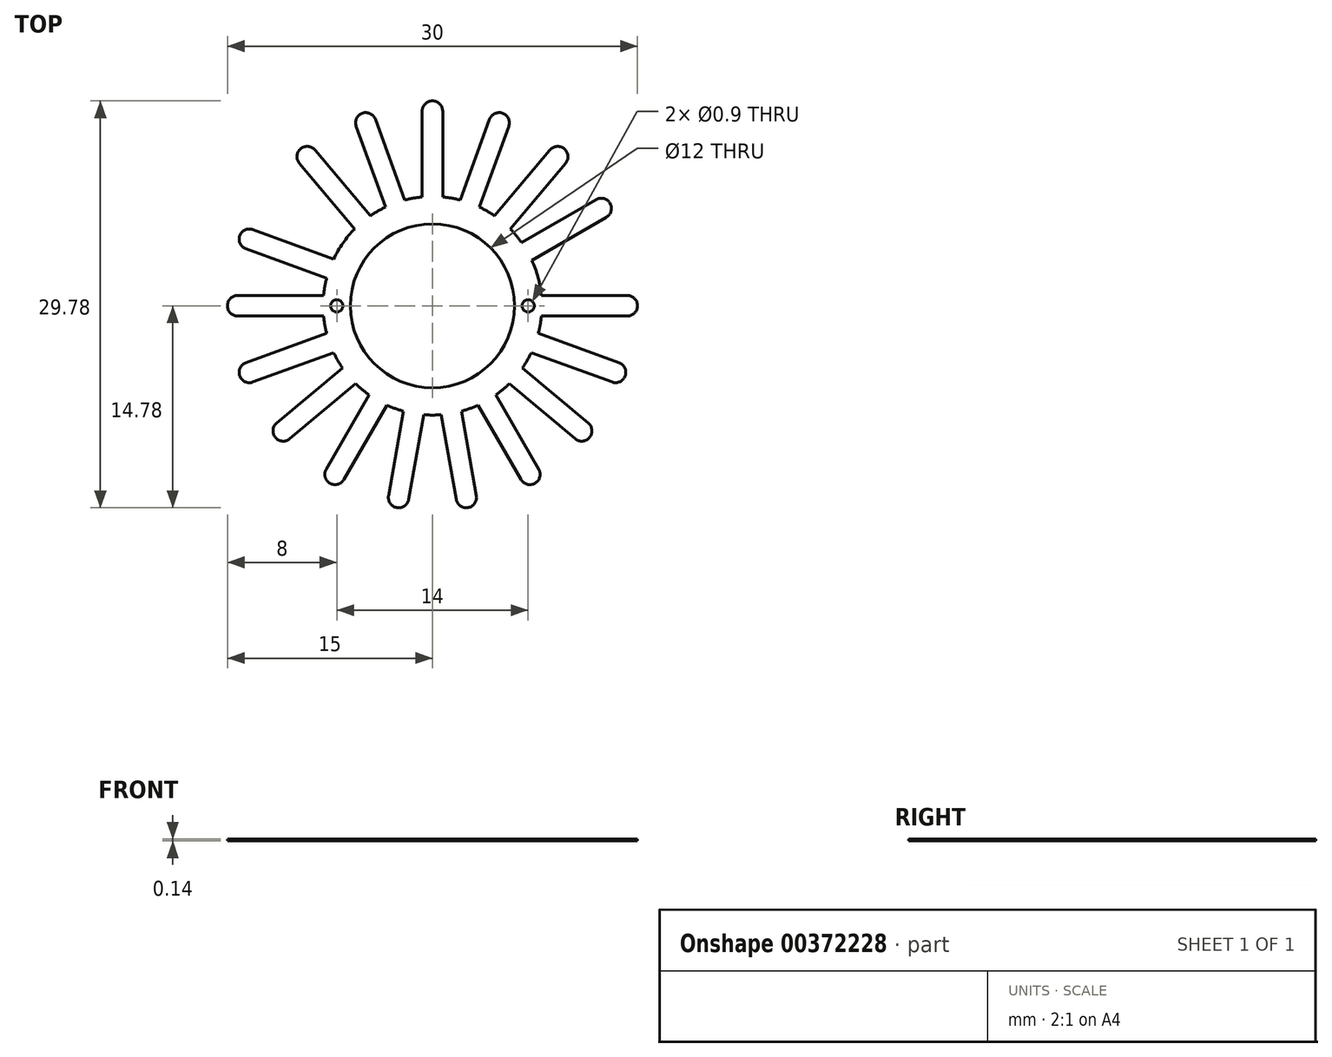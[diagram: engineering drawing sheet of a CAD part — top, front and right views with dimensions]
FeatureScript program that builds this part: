
annotation { "Feature Type Name" : "Feature", "Feature Type Description" : "" }
export const myFeature = defineFeature(function(context is Context, id is Id, definition is map)
    precondition{}
    {
        {
            var Q0;
            Q0=qCreatedBy(makeId("Top.planeOp"),FACE);
            var sketch = newSketch(context, id + "F0", { "sketchPlane" : qUnion([Q0])});
            skCircle(sketch, "E0", {"center": v(0, 0) * mm, "radius": 6 * mm});
            skCircle(sketch, "E1", {"center": v(0, 0) * mm, "radius": 8 * mm});
            skSolve(sketch);
        }
        {
            var Q0;
            Q0=makeQuery(id+"F0.imprint","IMPRINT",FACE,{"disambiguationData":[TD([[makeQuery(id+"F0.imprint","IMPRINT",EDGE,{"derivedFrom":sQuery(id+"F0.wireOp",EDGE,"E0")}),-1.0]])]});
            extrude(context, id + "F1", {"entities" : qUnion([Q0]), "depth" : 0.14 * mm});
        }
        {
            var Q0;
            Q0=qCreatedBy(makeId("Top.planeOp"),FACE);
            var sketch = newSketch(context, id + "F2", { "sketchPlane" : qUnion([Q0])});
            skCircle(sketch, "E2", {"center": v(0, 0) * mm, "radius": 8 * mm, "construction": true});
            skCircle(sketch, "E3", {"center": v(0, 0) * mm, "radius": 15 * mm, "construction": true});
            skArc(sketch, "E4", {"start": v(14.25, -0.75) * mm, "mid": v(15, 0) * mm, "end": v(14.25, 0.75) * mm});
            skLineSegment(sketch, "E5", {"start": v(14.25, -0.75) * mm, "end": v(7.96, -0.75) * mm});
            skLineSegment(sketch, "E6", {"start": v(14.25, 0.75) * mm, "end": v(7.96, 0.75) * mm});
            skLineSegment(sketch, "E7", {"start": v(7.96, 0.75) * mm, "end": v(7.96, -0.75) * mm});
            skSolve(sketch);
        }
        {
            var Q0;
            Q0=makeQuery(id+"F2.imprint","IMPRINT",FACE,{"disambiguationData":[TD([[makeQuery(id+"F2.imprint","IMPRINT",EDGE,{"derivedFrom":sQuery(id+"F2.wireOp",EDGE,"E4")}),1.0]])]});
            extrude(context, id + "F3", {"entities" : qUnion([Q0]), "depth" : 0.14 * mm});
        }
        {
            var Q0;
            Q0=qCreatedBy(makeId("Front.planeOp"),FACE);
            var sketch = newSketch(context, id + "F4", { "sketchPlane" : qUnion([Q0])});
            skLineSegment(sketch, "E8", {"start": v(0, 0) * mm, "end": v(0, 5.33) * mm, "construction": true});
            skSolve(sketch);
        }
        {
            var Q0;
            Q0=makeQuery(id+"F3.opExtrude","SWEPT_BODY",BODY,{"disambiguationData":[OSD([sQuery(id+"F2.wireOp",EDGE,"E4"),sQuery(id+"F2.wireOp",EDGE,"E5"),sQuery(id+"F2.wireOp",EDGE,"E6"),sQuery(id+"F2.wireOp",EDGE,"E7")])]});
            var Q1;
            Q1=sQuery(id+"F4.wireOp",EDGE,"E8");
            circularPattern(context, id + "F5", {"entities" : qUnion([Q0]), "axis" : qUnion([Q1]), "angle" : 20 * degree, "instanceCount" : 11, "oppositeDirection" : true, "computeTransformsWithoutBuiltin" : true});
        }
        {
            var Q0;
            Q0=qCreatedBy(makeId("Top.planeOp"),FACE);
            var sketch = newSketch(context, id + "F6", { "sketchPlane" : qUnion([Q0])});
            skCircle(sketch, "E9", {"center": v(0, 0) * mm, "radius": 15 * mm, "construction": true});
            skLineSegment(sketch, "E10", {"start": v(0, 0) * mm, "end": v(13, 7.5) * mm, "construction": true});
            skLineSegment(sketch, "E11", {"start": v(0, 0) * mm, "end": v(13.86, 0) * mm, "construction": true});
            skArc(sketch, "E12", {"start": v(12.72, 6.48) * mm, "mid": v(13, 7.5) * mm, "end": v(11.97, 7.77) * mm});
            skLineSegment(sketch, "E13", {"start": v(12.34, 7.13) * mm, "end": v(12.72, 6.48) * mm});
            skLineSegment(sketch, "E14", {"start": v(12.72, 6.48) * mm, "end": v(6.65, 2.98) * mm});
            skLineSegment(sketch, "E15", {"start": v(6.65, 2.98) * mm, "end": v(5.9, 4.27) * mm});
            skLineSegment(sketch, "E16", {"start": v(5.9, 4.27) * mm, "end": v(11.97, 7.77) * mm});
            skSolve(sketch);
        }
        {
            var Q0;
            Q0=makeQuery(id+"F6.imprint","IMPRINT",FACE,{"disambiguationData":[TD([[makeQuery(id+"F6.imprint","IMPRINT",EDGE,{"derivedFrom":sQuery(id+"F6.wireOp",EDGE,"E12")}),1.0]])]});
            extrude(context, id + "F7", {"entities" : qUnion([Q0]), "depth" : 0.14 * mm});
        }
        {
            var Q0;
            Q0=makeQuery(id+"F7.opExtrude","SWEPT_BODY",BODY,{"disambiguationData":[OSD([sQuery(id+"F6.wireOp",EDGE,"E12"),sQuery(id+"F6.wireOp",EDGE,"E14"),sQuery(id+"F6.wireOp",EDGE,"E15"),sQuery(id+"F6.wireOp",EDGE,"E16")])]});
            var Q1;
            Q1=sQuery(id+"F4.wireOp",EDGE,"E8");
            circularPattern(context, id + "F8", {"entities" : qUnion([Q0]), "axis" : qUnion([Q1]), "angle" : 20 * degree, "instanceCount" : 6, "computeTransformsWithoutBuiltin" : true});
        }
        {
            var Q0;
            Q0=makeQuery(id+"F1.opExtrude","SWEPT_BODY",BODY,{"disambiguationData":[OSD([sQuery(id+"F0.wireOp",EDGE,"E0"),sQuery(id+"F0.wireOp",EDGE,"E1")])]});
            var Q1;
            Q1=makeQuery(id+"F7.opExtrude","SWEPT_BODY",BODY,{"disambiguationData":[OSD([sQuery(id+"F6.wireOp",EDGE,"E12"),sQuery(id+"F6.wireOp",EDGE,"E14"),sQuery(id+"F6.wireOp",EDGE,"E15"),sQuery(id+"F6.wireOp",EDGE,"E16")])]});
            var Q2;
            Q2=makeQuery(id+"F8.opPattern","COPY",BODY,{"derivedFrom":makeQuery(id+"F7.opExtrude","SWEPT_BODY",BODY,{"disambiguationData":[OSD([sQuery(id+"F6.wireOp",EDGE,"E12"),sQuery(id+"F6.wireOp",EDGE,"E14"),sQuery(id+"F6.wireOp",EDGE,"E15"),sQuery(id+"F6.wireOp",EDGE,"E16")])]}),"instanceName":"1"});
            var Q3;
            Q3=makeQuery(id+"F8.opPattern","COPY",BODY,{"derivedFrom":makeQuery(id+"F7.opExtrude","SWEPT_BODY",BODY,{"disambiguationData":[OSD([sQuery(id+"F6.wireOp",EDGE,"E12"),sQuery(id+"F6.wireOp",EDGE,"E14"),sQuery(id+"F6.wireOp",EDGE,"E15"),sQuery(id+"F6.wireOp",EDGE,"E16")])]}),"instanceName":"2"});
            var Q4;
            Q4=makeQuery(id+"F8.opPattern","COPY",BODY,{"derivedFrom":makeQuery(id+"F7.opExtrude","SWEPT_BODY",BODY,{"disambiguationData":[OSD([sQuery(id+"F6.wireOp",EDGE,"E12"),sQuery(id+"F6.wireOp",EDGE,"E14"),sQuery(id+"F6.wireOp",EDGE,"E15"),sQuery(id+"F6.wireOp",EDGE,"E16")])]}),"instanceName":"3"});
            var Q5;
            Q5=makeQuery(id+"F8.opPattern","COPY",BODY,{"derivedFrom":makeQuery(id+"F7.opExtrude","SWEPT_BODY",BODY,{"disambiguationData":[OSD([sQuery(id+"F6.wireOp",EDGE,"E12"),sQuery(id+"F6.wireOp",EDGE,"E14"),sQuery(id+"F6.wireOp",EDGE,"E15"),sQuery(id+"F6.wireOp",EDGE,"E16")])]}),"instanceName":"4"});
            var Q6;
            Q6=makeQuery(id+"F8.opPattern","COPY",BODY,{"derivedFrom":makeQuery(id+"F7.opExtrude","SWEPT_BODY",BODY,{"disambiguationData":[OSD([sQuery(id+"F6.wireOp",EDGE,"E12"),sQuery(id+"F6.wireOp",EDGE,"E14"),sQuery(id+"F6.wireOp",EDGE,"E15"),sQuery(id+"F6.wireOp",EDGE,"E16")])]}),"instanceName":"5"});
            var Q7;
            Q7=makeQuery(id+"F5.opPattern","COPY",BODY,{"derivedFrom":makeQuery(id+"F3.opExtrude","SWEPT_BODY",BODY,{"disambiguationData":[OSD([sQuery(id+"F2.wireOp",EDGE,"E4"),sQuery(id+"F2.wireOp",EDGE,"E5"),sQuery(id+"F2.wireOp",EDGE,"E6"),sQuery(id+"F2.wireOp",EDGE,"E7")])]}),"instanceName":"10"});
            var Q8;
            Q8=makeQuery(id+"F5.opPattern","COPY",BODY,{"derivedFrom":makeQuery(id+"F3.opExtrude","SWEPT_BODY",BODY,{"disambiguationData":[OSD([sQuery(id+"F2.wireOp",EDGE,"E4"),sQuery(id+"F2.wireOp",EDGE,"E5"),sQuery(id+"F2.wireOp",EDGE,"E6"),sQuery(id+"F2.wireOp",EDGE,"E7")])]}),"instanceName":"9"});
            var Q9;
            Q9=makeQuery(id+"F5.opPattern","COPY",BODY,{"derivedFrom":makeQuery(id+"F3.opExtrude","SWEPT_BODY",BODY,{"disambiguationData":[OSD([sQuery(id+"F2.wireOp",EDGE,"E4"),sQuery(id+"F2.wireOp",EDGE,"E5"),sQuery(id+"F2.wireOp",EDGE,"E6"),sQuery(id+"F2.wireOp",EDGE,"E7")])]}),"instanceName":"8"});
            var Q10;
            Q10=makeQuery(id+"F5.opPattern","COPY",BODY,{"derivedFrom":makeQuery(id+"F3.opExtrude","SWEPT_BODY",BODY,{"disambiguationData":[OSD([sQuery(id+"F2.wireOp",EDGE,"E4"),sQuery(id+"F2.wireOp",EDGE,"E5"),sQuery(id+"F2.wireOp",EDGE,"E6"),sQuery(id+"F2.wireOp",EDGE,"E7")])]}),"instanceName":"7"});
            var Q11;
            Q11=makeQuery(id+"F5.opPattern","COPY",BODY,{"derivedFrom":makeQuery(id+"F3.opExtrude","SWEPT_BODY",BODY,{"disambiguationData":[OSD([sQuery(id+"F2.wireOp",EDGE,"E4"),sQuery(id+"F2.wireOp",EDGE,"E5"),sQuery(id+"F2.wireOp",EDGE,"E6"),sQuery(id+"F2.wireOp",EDGE,"E7")])]}),"instanceName":"6"});
            var Q12;
            Q12=makeQuery(id+"F5.opPattern","COPY",BODY,{"derivedFrom":makeQuery(id+"F3.opExtrude","SWEPT_BODY",BODY,{"disambiguationData":[OSD([sQuery(id+"F2.wireOp",EDGE,"E4"),sQuery(id+"F2.wireOp",EDGE,"E5"),sQuery(id+"F2.wireOp",EDGE,"E6"),sQuery(id+"F2.wireOp",EDGE,"E7")])]}),"instanceName":"4"});
            var Q13;
            Q13=makeQuery(id+"F5.opPattern","COPY",BODY,{"derivedFrom":makeQuery(id+"F3.opExtrude","SWEPT_BODY",BODY,{"disambiguationData":[OSD([sQuery(id+"F2.wireOp",EDGE,"E4"),sQuery(id+"F2.wireOp",EDGE,"E5"),sQuery(id+"F2.wireOp",EDGE,"E6"),sQuery(id+"F2.wireOp",EDGE,"E7")])]}),"instanceName":"5"});
            var Q14;
            Q14=makeQuery(id+"F5.opPattern","COPY",BODY,{"derivedFrom":makeQuery(id+"F3.opExtrude","SWEPT_BODY",BODY,{"disambiguationData":[OSD([sQuery(id+"F2.wireOp",EDGE,"E4"),sQuery(id+"F2.wireOp",EDGE,"E5"),sQuery(id+"F2.wireOp",EDGE,"E6"),sQuery(id+"F2.wireOp",EDGE,"E7")])]}),"instanceName":"3"});
            var Q15;
            Q15=makeQuery(id+"F5.opPattern","COPY",BODY,{"derivedFrom":makeQuery(id+"F3.opExtrude","SWEPT_BODY",BODY,{"disambiguationData":[OSD([sQuery(id+"F2.wireOp",EDGE,"E4"),sQuery(id+"F2.wireOp",EDGE,"E5"),sQuery(id+"F2.wireOp",EDGE,"E6"),sQuery(id+"F2.wireOp",EDGE,"E7")])]}),"instanceName":"2"});
            var Q16;
            Q16=makeQuery(id+"F5.opPattern","COPY",BODY,{"derivedFrom":makeQuery(id+"F3.opExtrude","SWEPT_BODY",BODY,{"disambiguationData":[OSD([sQuery(id+"F2.wireOp",EDGE,"E4"),sQuery(id+"F2.wireOp",EDGE,"E5"),sQuery(id+"F2.wireOp",EDGE,"E6"),sQuery(id+"F2.wireOp",EDGE,"E7")])]}),"instanceName":"1"});
            var Q17;
            Q17=makeQuery(id+"F3.opExtrude","SWEPT_BODY",BODY,{"disambiguationData":[OSD([sQuery(id+"F2.wireOp",EDGE,"E4"),sQuery(id+"F2.wireOp",EDGE,"E5"),sQuery(id+"F2.wireOp",EDGE,"E6"),sQuery(id+"F2.wireOp",EDGE,"E7")])]});
            booleanBodies(context, id + "F9", {"operationType" : BooleanOperationType.UNION, "tools" : qUnion([Q0, Q1, Q2, Q3, Q4, Q5, Q6, Q7, Q8, Q9, Q10, Q11, Q12, Q13, Q14, Q15, Q16, Q17])});
        }
        {
            var Q0;
            {var subQ0=makeQuery(id+"F3.opExtrude","CAP_FACE",FACE,{"disambiguationData":[OSD([sQuery(id+"F2.wireOp",EDGE,"E4"),sQuery(id+"F2.wireOp",EDGE,"E5"),sQuery(id+"F2.wireOp",EDGE,"E6"),sQuery(id+"F2.wireOp",EDGE,"E7")])],"isStart":false});var subQ1=makeQuery(id+"F7.opExtrude","CAP_FACE",FACE,{"disambiguationData":[OSD([sQuery(id+"F6.wireOp",EDGE,"E12"),sQuery(id+"F6.wireOp",EDGE,"E14"),sQuery(id+"F6.wireOp",EDGE,"E15"),sQuery(id+"F6.wireOp",EDGE,"E16")])],"isStart":false});Q0=makeQuery(id+"F9.opBoolean","MERGE",FACE,{"derivedFrom":[makeQuery(id+"F1.opExtrude","CAP_FACE",FACE,{"disambiguationData":[OSD([sQuery(id+"F0.wireOp",EDGE,"E0"),sQuery(id+"F0.wireOp",EDGE,"E1")])],"isStart":false}),subQ0,makeQuery(id+"F5.opPattern","COPY",FACE,{"derivedFrom":subQ0,"instanceName":"1"}),makeQuery(id+"F5.opPattern","COPY",FACE,{"derivedFrom":subQ0,"instanceName":"2"}),makeQuery(id+"F5.opPattern","COPY",FACE,{"derivedFrom":subQ0,"instanceName":"3"}),makeQuery(id+"F5.opPattern","COPY",FACE,{"derivedFrom":subQ0,"instanceName":"4"}),makeQuery(id+"F5.opPattern","COPY",FACE,{"derivedFrom":subQ0,"instanceName":"5"}),makeQuery(id+"F5.opPattern","COPY",FACE,{"derivedFrom":subQ0,"instanceName":"6"}),makeQuery(id+"F5.opPattern","COPY",FACE,{"derivedFrom":subQ0,"instanceName":"7"}),makeQuery(id+"F5.opPattern","COPY",FACE,{"derivedFrom":subQ0,"instanceName":"8"}),makeQuery(id+"F5.opPattern","COPY",FACE,{"derivedFrom":subQ0,"instanceName":"9"}),makeQuery(id+"F5.opPattern","COPY",FACE,{"derivedFrom":subQ0,"instanceName":"10"}),subQ1,makeQuery(id+"F8.opPattern","COPY",FACE,{"derivedFrom":subQ1,"instanceName":"1"}),makeQuery(id+"F8.opPattern","COPY",FACE,{"derivedFrom":subQ1,"instanceName":"2"}),makeQuery(id+"F8.opPattern","COPY",FACE,{"derivedFrom":subQ1,"instanceName":"3"}),makeQuery(id+"F8.opPattern","COPY",FACE,{"derivedFrom":subQ1,"instanceName":"4"}),makeQuery(id+"F8.opPattern","COPY",FACE,{"derivedFrom":subQ1,"instanceName":"5"})]});}
            var sketch = newSketch(context, id + "F10", { "sketchPlane" : qUnion([Q0])});
            skCircle(sketch, "E17", {"center": v(0, 0) * mm, "radius": 7 * mm, "construction": true});
            skCircle(sketch, "E18", {"center": v(7, 0) * mm, "radius": 0.45 * mm});
            skCircle(sketch, "E19", {"center": v(-7, 0) * mm, "radius": 0.45 * mm});
            skSolve(sketch);
        }
        {
            var Q0;
            {Q0=qUnion([makeQuery(id+"F10.imprint","IMPRINT",FACE,{"disambiguationData":[TD([[makeQuery(id+"F10.imprint","IMPRINT",EDGE,{"derivedFrom":sQuery(id+"F10.wireOp",EDGE,"E18")}),1.0]])]}),makeQuery(id+"F10.imprint","IMPRINT",FACE,{"disambiguationData":[TD([[makeQuery(id+"F10.imprint","IMPRINT",EDGE,{"derivedFrom":sQuery(id+"F10.wireOp",EDGE,"E19")}),1.0]])]})]);}
            extrude(context, id + "F11", {"entities" : qUnion([Q0]), "operationType" : NewBodyOperationType.REMOVE, "oppositeDirection" : true, "depth" : 0.14 * mm});
        }
    });
